# Revit family: ADB Warming cabinet CES 505
name_source: partatom
category: Equipement spécialisé
units: mm (PartAtom-declared; Revit-internal decimal feet)

## family parameters
Basée sur le plan de construction = Non
Conserver l'orientation des annotations = Non
Cote de connecteur circulaire = Utiliser le diamètre
Couper avec des vides une fois chargée = Non
Partagée = Non
Repère de localisation dans la pièce = Non
Toujours verticalement = Oui
Type d'élément = Normal

## types (1)
- CES 505
    Commentaires du type = Ambassade range - Convection ovens
    Cycle = 50 Hz
    Depth = 686 mm  [stored 2.25066 ft]
    Description = Warming cabinet for CFE505CT oven
    Electric Connection Type = Bornier 40A
    Electric power = 950 W
    Electrical Remarks = 230V(MONO) commutable 400V(TRI)
    Elévation par défaut = 0 mm  [stored 0 ft]
    F = 750 mm  [stored 2.46063 ft]
    Fabricant = Société Industrielle  de Lacanche
    G = 250 mm  [stored 0.82021 ft]
    Height = 910 mm
    Length = 500 mm  [stored 1.64042 ft]
    Modèle = CES 505
    Number of Poles = 1
    Operational Current = 4 A
    Phase = 1
    URL = https://www.ambassade-de-bourgogne.com
    Volts = 230 V
    Weight = 54.00 kg

note: [stored X ft] marks values corroborated as IEEE doubles in the binary element streams (Revit-internal decimal feet)
